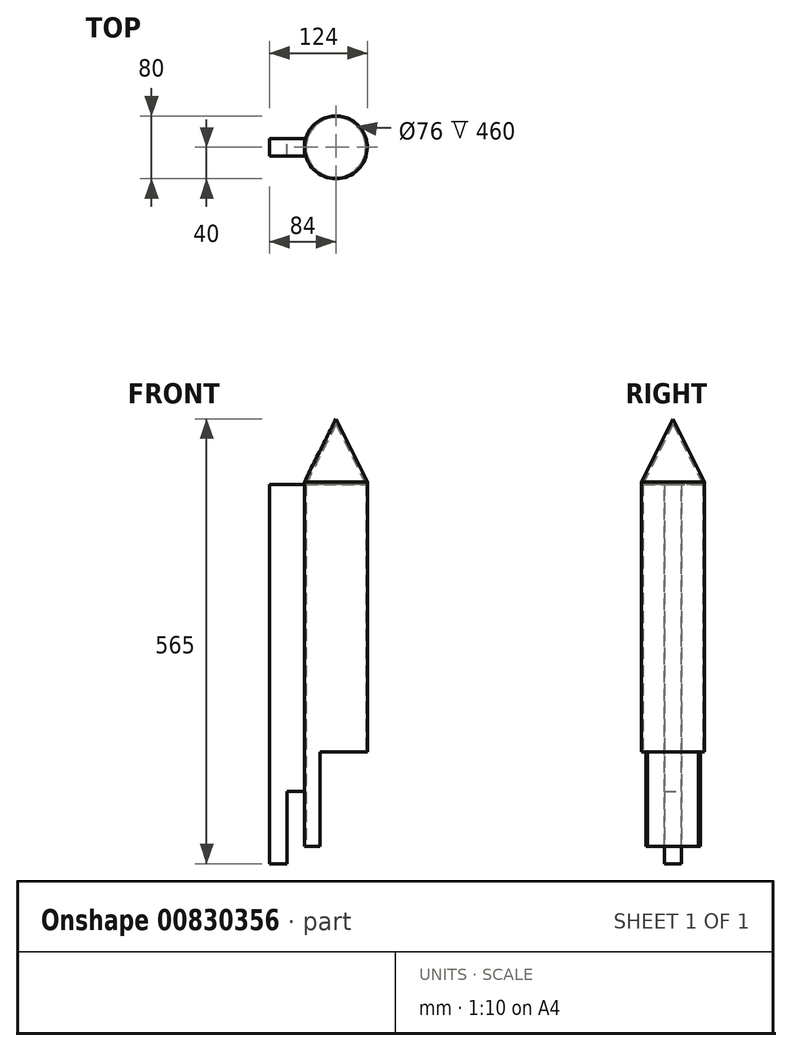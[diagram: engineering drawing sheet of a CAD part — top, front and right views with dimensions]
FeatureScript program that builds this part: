
annotation { "Feature Type Name" : "Feature", "Feature Type Description" : "" }
export const myFeature = defineFeature(function(context is Context, id is Id, definition is map)
    precondition{}
    {
        {
            var Q0;
            Q0=qCreatedBy(makeId("Top.planeOp"),FACE);
            var sketch = newSketch(context, id + "F0", { "sketchPlane" : qUnion([Q0])});
            skCircle(sketch, "E0", {"center": v(0, 0) * mm, "radius": 40 * mm});
            skCircle(sketch, "E1", {"center": v(0, 0) * mm, "radius": 38 * mm});
            skSolve(sketch);
        }
        {
            var Q0;
            Q0=makeQuery(id+"F0.imprint","IMPRINT",FACE,{"disambiguationData":[TD([[makeQuery(id+"F0.imprint","IMPRINT",EDGE,{"derivedFrom":sQuery(id+"F0.wireOp",EDGE,"E0")}),1.0]])]});
            extrude(context, id + "F1", {"entities" : qUnion([Q0]), "depth" : 460 * mm, "offsetDistance" : 25 * mm});
        }
        {
            var Q0;
            Q0=qCreatedBy(makeId("Front.planeOp"),FACE);
            var sketch = newSketch(context, id + "F2", { "sketchPlane" : qUnion([Q0])});
            skLineSegment(sketch, "E2.bottom", {"start": v(40, 0) * mm, "end": v(-20, 0) * mm});
            skLineSegment(sketch, "E2.top", {"start": v(40, 120) * mm, "end": v(-20, 120) * mm});
            skLineSegment(sketch, "E2.left", {"start": v(40, 0) * mm, "end": v(40, 120) * mm});
            skLineSegment(sketch, "E2.right", {"start": v(-20, 0) * mm, "end": v(-20, 120) * mm});
            skLineSegment(sketch, "E3", {"start": v(-40, 0) * mm, "end": v(-40, 460) * mm, "construction": true});
            skLineSegment(sketch, "E4", {"start": v(40, 460) * mm, "end": v(40, 0) * mm, "construction": true});
            skSolve(sketch);
        }
        {
            var Q0;
            Q0 = qSketchRegion(id + "F2", true);
            extrude(context, id + "F3", {"entities" : qUnion([Q0]), "operationType" : NewBodyOperationType.REMOVE, "endBound" : BoundingType.SYMMETRIC, "oppositeDirection" : true, "depth" : 90 * mm, "offsetDistance" : 25 * mm});
        }
        {
            var Q0;
            Q0=qCreatedBy(makeId("Front.planeOp"),FACE);
            var sketch = newSketch(context, id + "F4", { "sketchPlane" : qUnion([Q0])});
            skLineSegment(sketch, "E5", {"start": v(0, 543) * mm, "end": v(40, 463) * mm});
            skLineSegment(sketch, "E6", {"start": v(40, 463) * mm, "end": v(40, 460) * mm});
            skLineSegment(sketch, "E7", {"start": v(40, 460) * mm, "end": v(40, 120) * mm, "construction": true});
            skLineSegment(sketch, "E8", {"start": v(0, 543) * mm, "end": v(0, 536.3) * mm});
            skLineSegment(sketch, "E9", {"start": v(0, 536.3) * mm, "end": v(38.15, 460) * mm});
            skLineSegment(sketch, "E10", {"start": v(38.15, 460) * mm, "end": v(40, 460) * mm});
            skSolve(sketch);
        }
        {
            var Q0;
            Q0=makeQuery(id+"F4.imprint","IMPRINT",FACE,{"disambiguationData":[TD([[makeQuery(id+"F4.imprint","IMPRINT",EDGE,{"derivedFrom":sQuery(id+"F4.wireOp",EDGE,"E5")}),-1.0]])]});
            var Q1;
            Q1=sQuery(id+"F4.wireOp",EDGE,"E8");
            revolve(context, id + "F5", {"operationType" : NewBodyOperationType.ADD, "surfaceOperationType" : NewSurfaceOperationType.NEW, "entities" : qUnion([Q0]), "axis" : qUnion([Q1]), "revolveType" : RevolveType.FULL});
        }
        {
            var Q0;
            Q0=qCreatedBy(makeId("Front.planeOp"),FACE);
            var sketch = newSketch(context, id + "F6", { "sketchPlane" : qUnion([Q0])});
            skLineSegment(sketch, "E11", {"start": v(-84, -22) * mm, "end": v(-84, 460) * mm});
            skLineSegment(sketch, "E12", {"start": v(-84, 460) * mm, "end": v(-40, 460) * mm});
            skLineSegment(sketch, "E13", {"start": v(-40, 460) * mm, "end": v(-40, 70) * mm});
            skLineSegment(sketch, "E14", {"start": v(-40, 70) * mm, "end": v(-62, 70) * mm});
            skLineSegment(sketch, "E15", {"start": v(-62, 70) * mm, "end": v(-62, -22) * mm});
            skLineSegment(sketch, "E16", {"start": v(-62, -22) * mm, "end": v(-84, -22) * mm});
            skLineSegment(sketch, "E17", {"start": v(-40, 0) * mm, "end": v(-40, 463) * mm, "construction": true});
            skLineSegment(sketch, "E18", {"start": v(40, 463) * mm, "end": v(40, 120) * mm, "construction": true});
            skSolve(sketch);
        }
        {
            var Q0;
            Q0=makeQuery(id+"F6.imprint","IMPRINT",FACE,{"disambiguationData":[TD([[makeQuery(id+"F6.imprint","IMPRINT",EDGE,{"derivedFrom":sQuery(id+"F6.wireOp",EDGE,"E11")}),-1.0]])]});
            extrude(context, id + "F7", {"entities" : qUnion([Q0]), "operationType" : NewBodyOperationType.ADD, "endBound" : BoundingType.SYMMETRIC, "depth" : 22 * mm, "offsetDistance" : 25 * mm});
        }
    });
